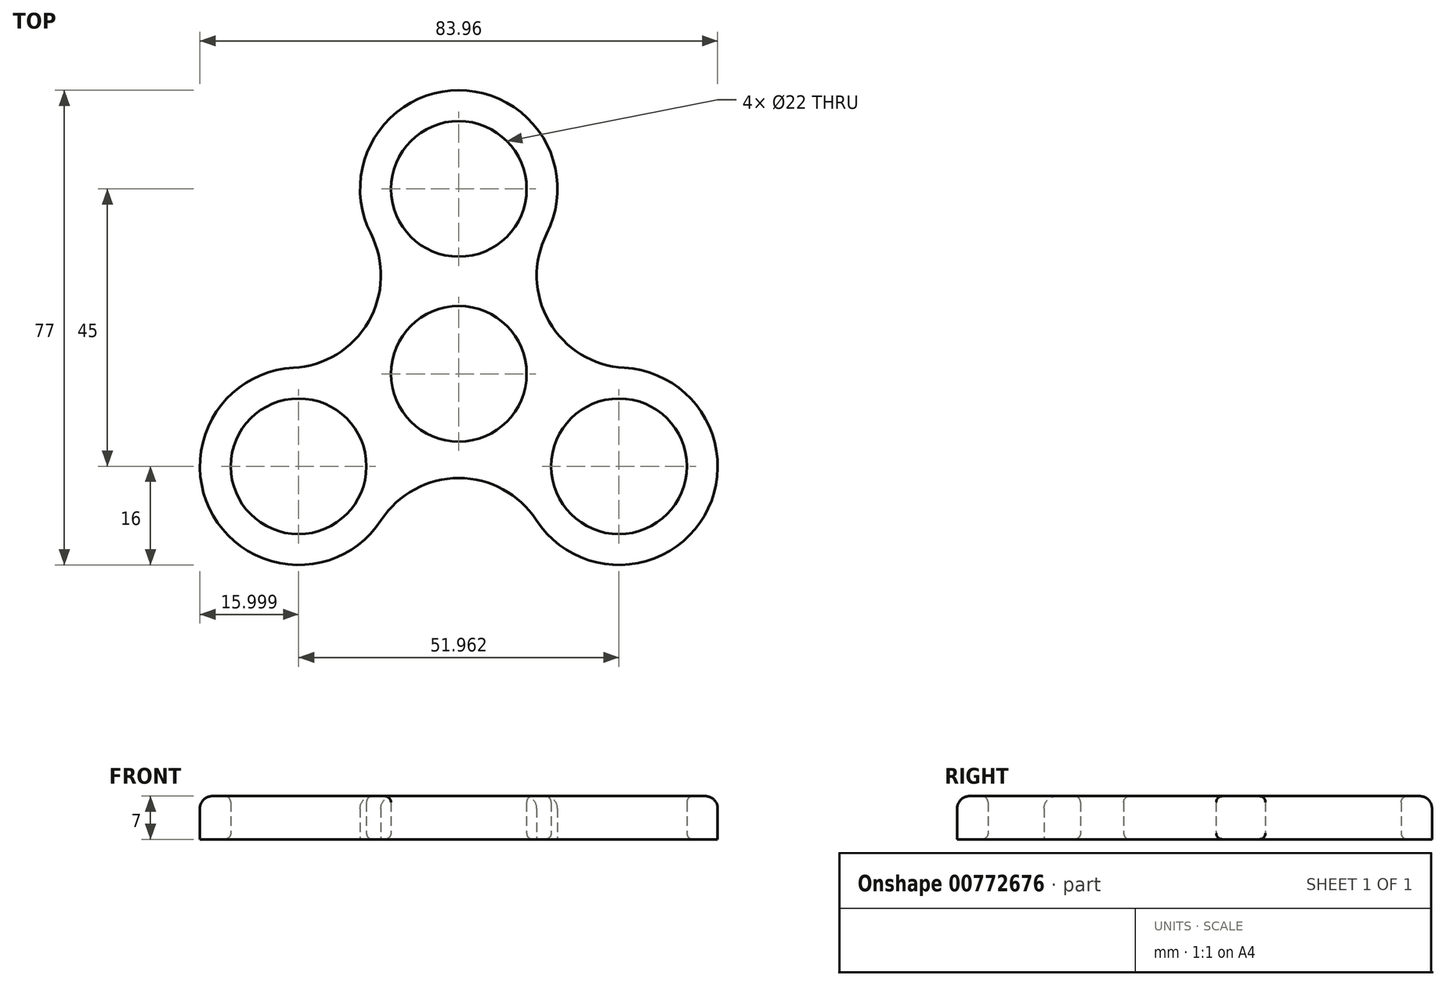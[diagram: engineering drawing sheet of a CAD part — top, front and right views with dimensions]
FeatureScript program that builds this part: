
annotation { "Feature Type Name" : "Feature", "Feature Type Description" : "" }
export const myFeature = defineFeature(function(context is Context, id is Id, definition is map)
    precondition{}
    {
        {
            var Q0;
            Q0=qCreatedBy(makeId("Top.planeOp"),FACE);
            var sketch = newSketch(context, id + "F0", { "sketchPlane" : qUnion([Q0])});
            skCircle(sketch, "E0", {"center": v(0, 0) * mm, "radius": 11 * mm});
            skCircle(sketch, "E1", {"center": v(0, 30) * mm, "radius": 11 * mm});
            skCircle(sketch, "E2.1.0", {"center": v(-25.98, -15) * mm, "radius": 11 * mm});
            skCircle(sketch, "E2.2.0", {"center": v(25.98, -15) * mm, "radius": 11 * mm});
            skArc(sketch, "E3", {"start": v(14.26, 22.75) * mm, "mid": v(0, 46) * mm, "end": v(-14.26, 22.75) * mm});
            skArc(sketch, "E4.1.0", {"start": v(-26.84, 0.98) * mm, "mid": v(-39.84, -23) * mm, "end": v(-12.57, -23.73) * mm});
            skArc(sketch, "E4.2.0", {"start": v(12.57, -23.73) * mm, "mid": v(39.84, -23) * mm, "end": v(26.84, 0.98) * mm});
            skArc(sketch, "E5", {"start": v(14.26, 22.75) * mm, "mid": v(14.65, 8.46) * mm, "end": v(26.84, 0.98) * mm});
            skArc(sketch, "E6.1.0", {"start": v(-26.84, 0.98) * mm, "mid": v(-14.65, 8.46) * mm, "end": v(-14.26, 22.75) * mm});
            skArc(sketch, "E6.2.0", {"start": v(12.57, -23.73) * mm, "mid": v(0, -16.91) * mm, "end": v(-12.57, -23.73) * mm});
            skSolve(sketch);
        }
        {
            var Q0;
            Q0 = qSketchRegion(id + "F0", true);
            extrude(context, id + "F1", {"entities" : qUnion([Q0]), "depth" : 7 * mm, "offsetDistance" : 25 * mm});
        }
        {
            var Q0;
            Q0=makeQuery(id+"F1.opExtrude","CAP_EDGE",EDGE,{"disambiguationData":[OSD([sQuery(id+"F0.wireOp",EDGE,"E1")])],"isStart":false});
            var Q1;
            Q1=makeQuery(id+"F1.opExtrude","CAP_EDGE",EDGE,{"disambiguationData":[OSD([sQuery(id+"F0.wireOp",EDGE,"E0")])],"isStart":false});
            var Q2;
            Q2=makeQuery(id+"F1.opExtrude","CAP_EDGE",EDGE,{"disambiguationData":[OSD([sQuery(id+"F0.wireOp",EDGE,"E2.2.0")])],"isStart":false});
            var Q3;
            Q3=makeQuery(id+"F1.opExtrude","CAP_EDGE",EDGE,{"disambiguationData":[OSD([sQuery(id+"F0.wireOp",EDGE,"E2.1.0")])],"isStart":false});
            var Q4;
            Q4=makeQuery(id+"F1.opExtrude","CAP_EDGE",EDGE,{"disambiguationData":[OSD([sQuery(id+"F0.wireOp",EDGE,"E2.1.0")])],"isStart":true});
            var Q5;
            Q5=makeQuery(id+"F1.opExtrude","CAP_EDGE",EDGE,{"disambiguationData":[OSD([sQuery(id+"F0.wireOp",EDGE,"E0")])],"isStart":true});
            var Q6;
            Q6=makeQuery(id+"F1.opExtrude","CAP_EDGE",EDGE,{"disambiguationData":[OSD([sQuery(id+"F0.wireOp",EDGE,"E2.2.0")])],"isStart":true});
            var Q7;
            Q7=makeQuery(id+"F1.opExtrude","CAP_EDGE",EDGE,{"disambiguationData":[OSD([sQuery(id+"F0.wireOp",EDGE,"E1")])],"isStart":true});
            fillet(context, id + "F2", {"entities" : qUnion([Q0, Q1, Q2, Q3, Q4, Q5, Q6, Q7]), "radius" : 1 * mm, "tangentPropagation" : true, "allowEdgeOverflow" : false});
        }
        {
            var Q0;
            Q0=makeQuery(id+"F1.opExtrude","CAP_EDGE",EDGE,{"disambiguationData":[OSD([sQuery(id+"F0.wireOp",EDGE,"E6.1.0")])],"isStart":false});
            fillet(context, id + "F3", {"entities" : qUnion([Q0]), "radius" : 2 * mm, "tangentPropagation" : true, "allowEdgeOverflow" : false});
        }
    });
